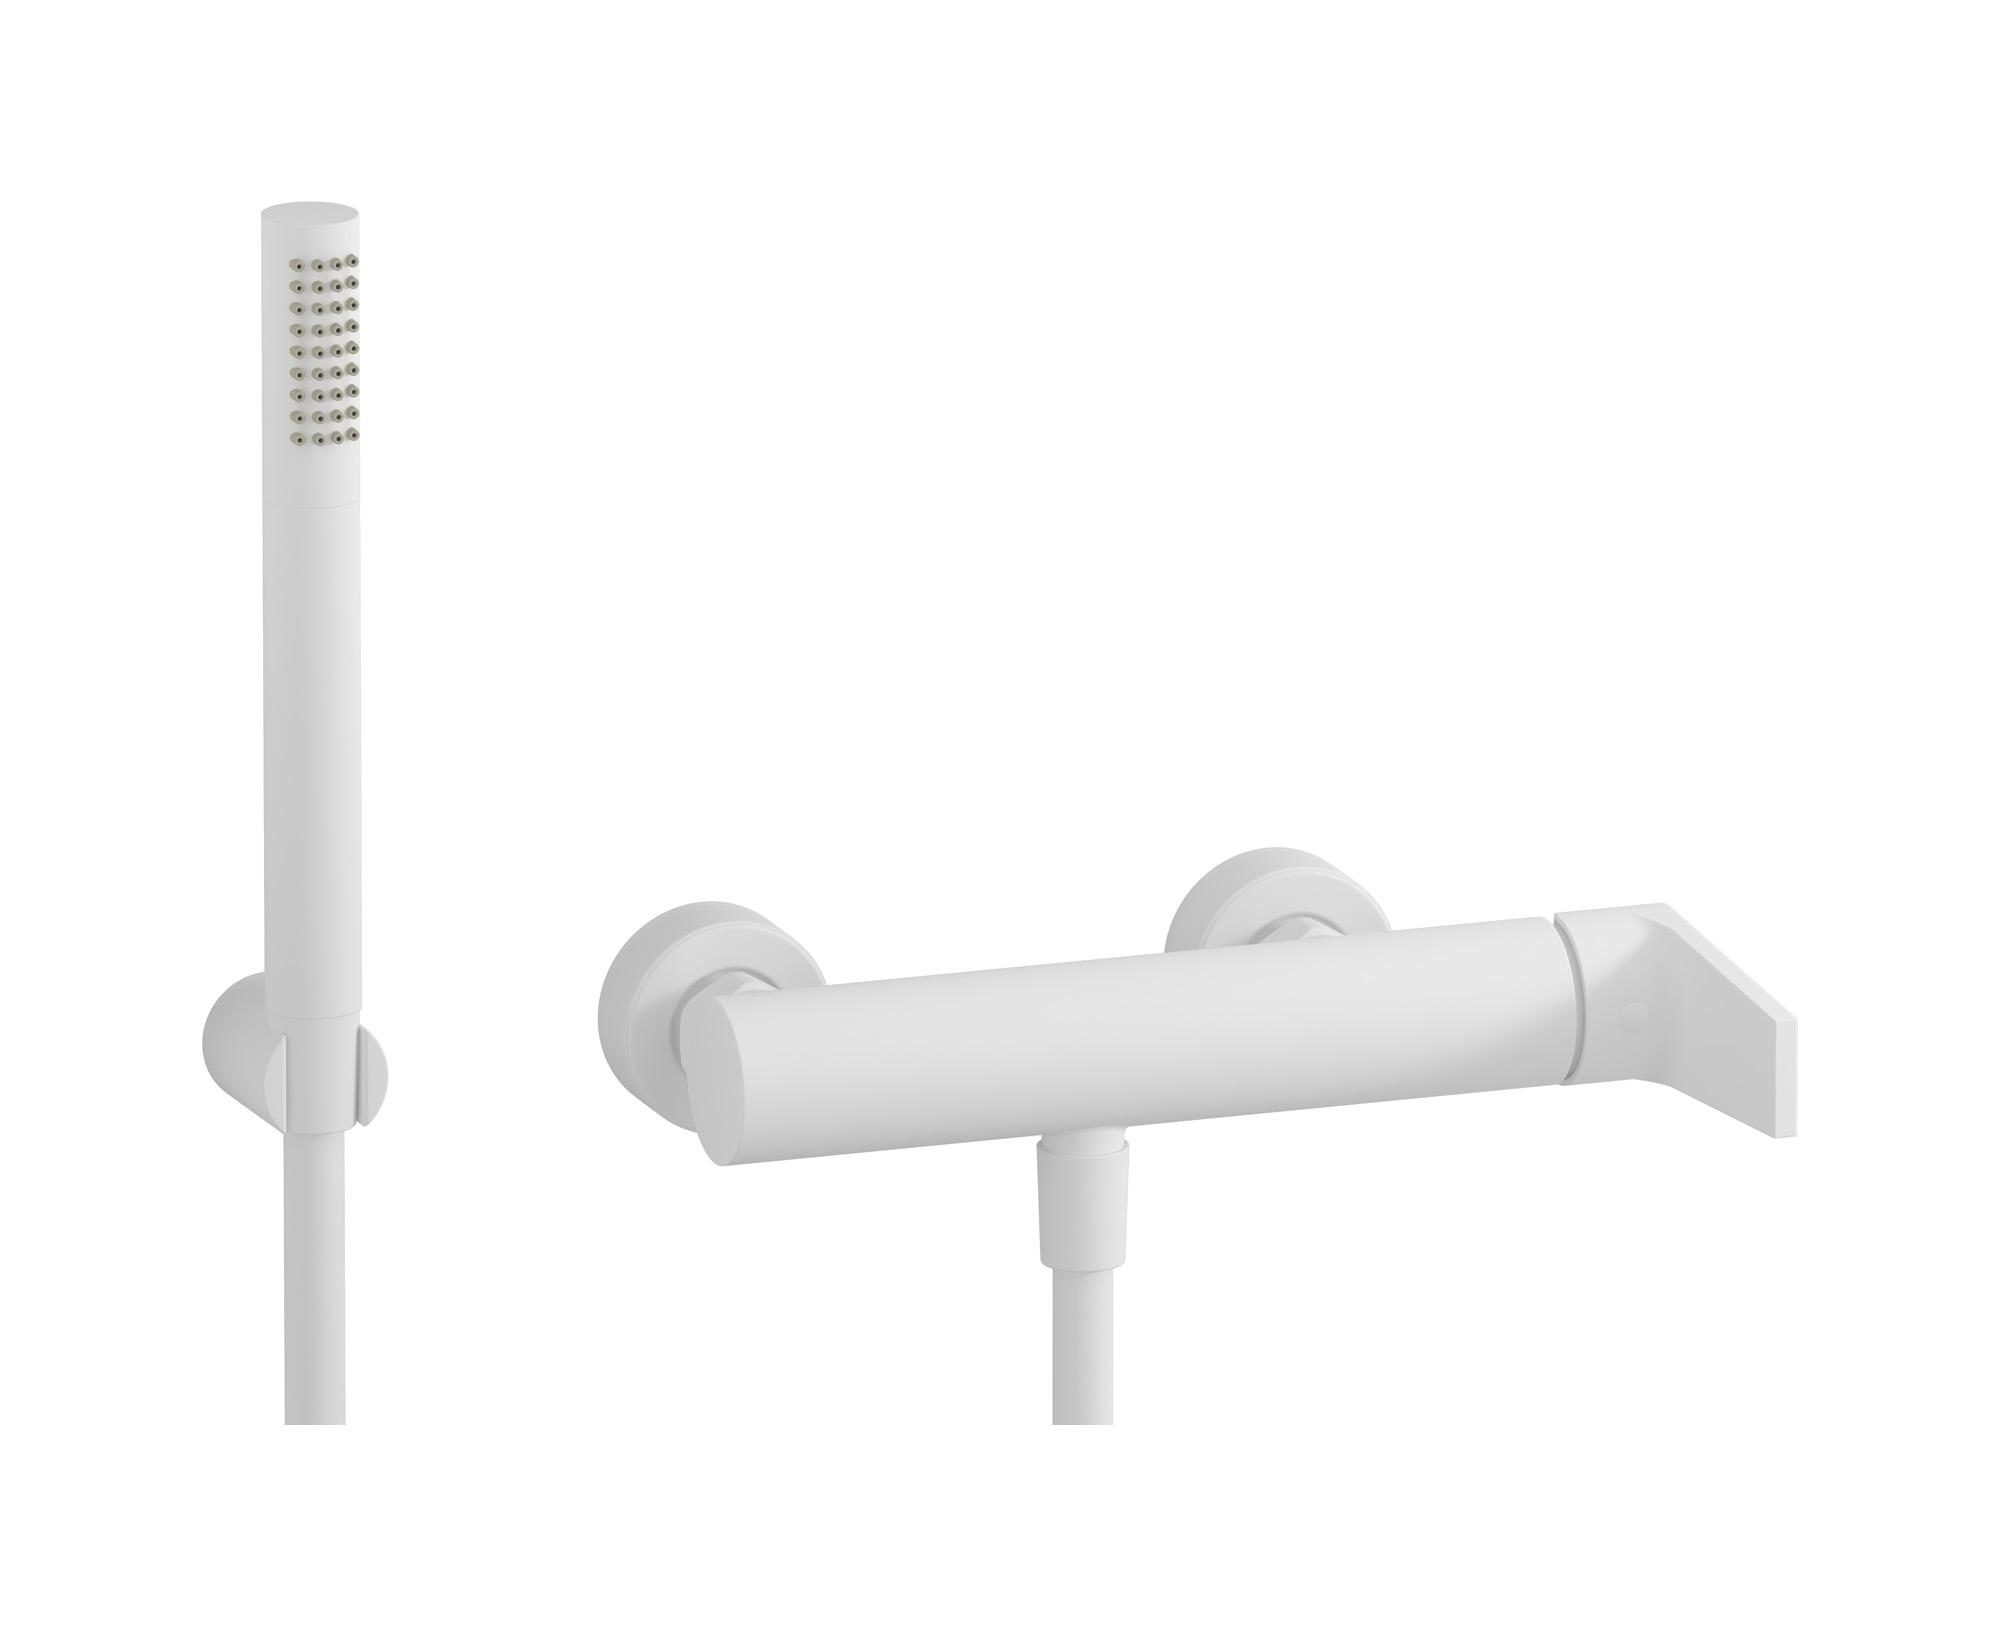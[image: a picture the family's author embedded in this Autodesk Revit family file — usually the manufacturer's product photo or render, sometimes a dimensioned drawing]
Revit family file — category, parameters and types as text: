
# Revit family: TW350
name_source: partatom
category: Apparecchi idraulici
units: mm (PartAtom-declared; Revit-internal decimal feet)

## family parameters
Basato su piano di lavoro = No
Condiviso = No
Mantieni orientamento annotazione = No
Numero OmniClass = 23.45.55.17
Punto di calcolo locali = No
Quota connettore circolare = Usa diametro
Sempre verticale = Sì
Taglio con vuoti quando caricato = No
Tipo di parte = Normale
Titolo OmniClass = Mixing Faucets

## types (12) — shared parameters
Cold water inlet = 10 mm  [stored 0.0328084 ft]
Commenti sul tipo = Bath filler
Connessione CW = No
Connessione HW = No
Connessione di scarico = No
Connessione di ventilazione = No
Descrizione = Wall mounted shower mixer with shower kit
Hot water inlet = 10 mm  [stored 0.0328084 ft]
Produttore = IB Rubinetterie S.p.A.
URL = https://www.weareib.it
zero-valued in all types: Prospetto di default

## per-type parameters (varying)
| type | Finishes surface | Immagine tipo | Modello |
| Chrome | IB_Chrome | TW350CC.jpg | TW350CC |
| Brushed nickel | IB_Brushed nickel | TW350SS.jpg | TW350SS |
| Matt white | IB_matt white | TW350BO.jpg | TW350BO |
| Matt black | IB_matt black | TW350NP.jpg | TW350NP |
| Black chrome | IB_Black chrome | TW350CF.jpg | TW350CF |
| Brushed black chrome | IB_Brushed black chrome | TW350CS.jpg | TW350CS |
| Pale gold | IB_Brushed black chrome | TW350II.jpg | TW350II |
| Brushed pale gold | IB_brushed pale gold | TW350IS.jpg | TW350IS |
| Rose gold | IB_Rose gold | TW350RS.jpg | TW350RS |
| Brushed rose gold | IB_Brushed rose gold | TW350SR.jpg | TW350SR |
| Gold | IB_gold | TW350OO.jpg | TW350OO |
| Brushed gold | IB_brushed gold | TW350OS.jpg | TW350OS |

note: [stored X ft] marks values corroborated as IEEE doubles in the binary element streams (Revit-internal decimal feet)
